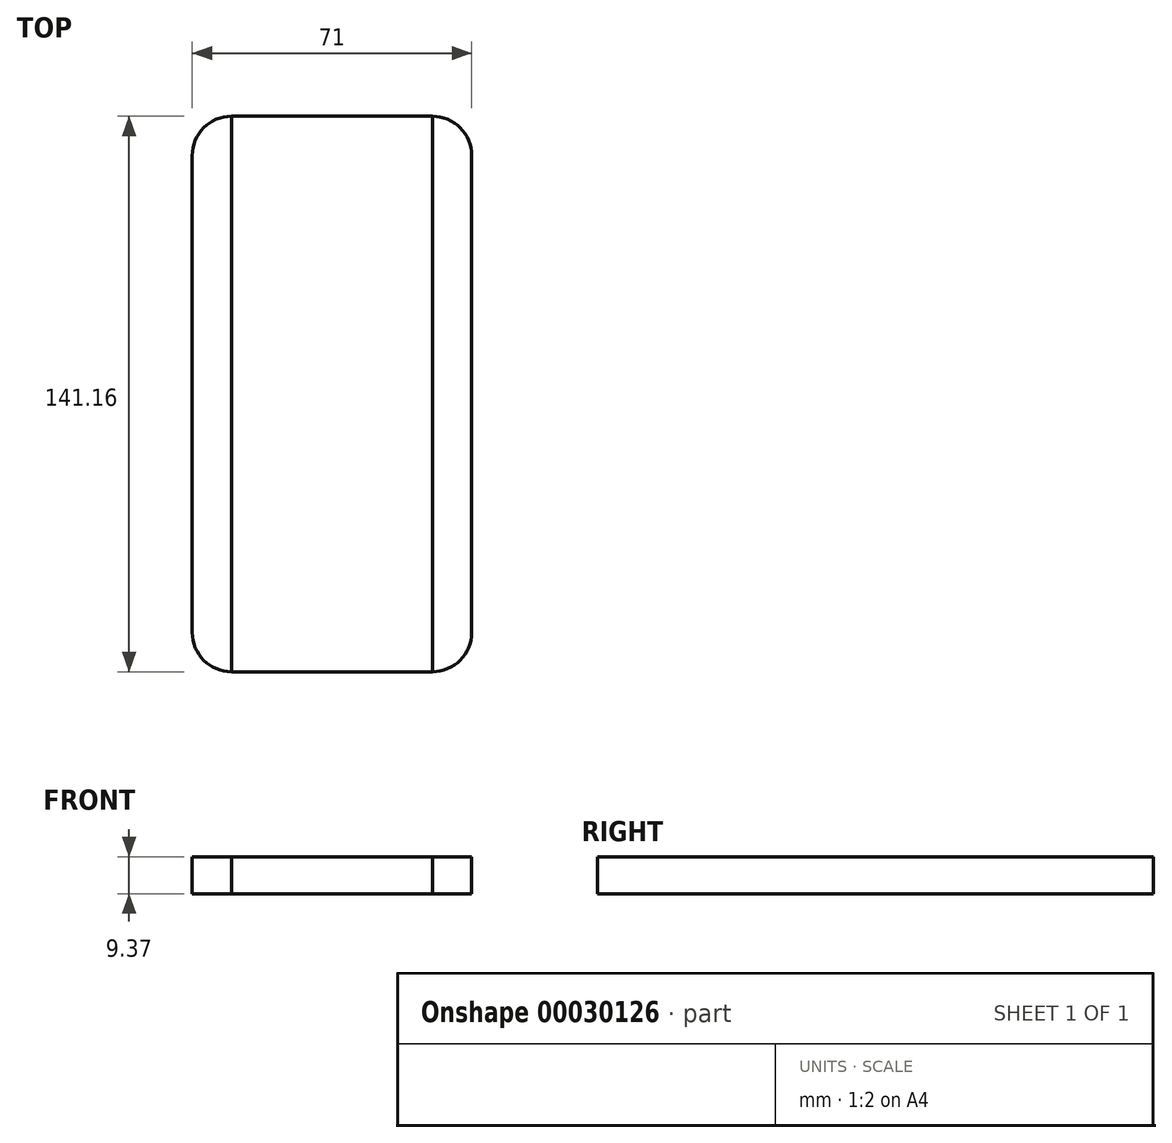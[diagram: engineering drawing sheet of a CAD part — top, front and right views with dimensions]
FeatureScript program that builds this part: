
annotation { "Feature Type Name" : "Feature", "Feature Type Description" : "" }
export const myFeature = defineFeature(function(context is Context, id is Id, definition is map)
    precondition{}
    {
        {
            var Q0;
            Q0=qCreatedBy(makeId("Top.planeOp"),FACE);
            var sketch = newSketch(context, id + "F0", { "sketchPlane" : qUnion([Q0])});
            skLineSegment(sketch, "E0.rect.bottom", {"start": v(35.5, -70.58) * mm, "end": v(-35.5, -70.58) * mm});
            skLineSegment(sketch, "E0.rect.top", {"start": v(35.5, 70.58) * mm, "end": v(-35.5, 70.58) * mm});
            skLineSegment(sketch, "E0.rect.left", {"start": v(35.5, -70.58) * mm, "end": v(35.5, 70.58) * mm});
            skLineSegment(sketch, "E0.rect.right", {"start": v(-35.5, -70.58) * mm, "end": v(-35.5, 70.57) * mm});
            skPoint(sketch, "E0.rect.middle", {"position": v(0, 0) * mm});
            skSolve(sketch);
        }
        {
            var Q0;
            Q0=makeQuery(id+"F0.imprint","IMPRINT",FACE,{"disambiguationData":[TD([[makeQuery(id+"F0.imprint","IMPRINT",EDGE,{"derivedFrom":sQuery(id+"F0.wireOp",EDGE,"E0.rect.bottom")}),-1.0]])]});
            extrude(context, id + "F1", {"entities" : qUnion([Q0]), "depth" : 9.37 * mm});
        }
        {
            var Q0;
            Q0=makeQuery(id+"F1.opExtrude","SWEPT_EDGE",EDGE,{"disambiguationData":[OSD([sQuery(id+"F0.wireOp",EDGE,"E0.rect.bottom"),sQuery(id+"F0.wireOp",EDGE,"E0.rect.left")])]});
            var Q1;
            Q1=makeQuery(id+"F1.opExtrude","SWEPT_EDGE",EDGE,{"disambiguationData":[OSD([sQuery(id+"F0.wireOp",EDGE,"E0.rect.bottom"),sQuery(id+"F0.wireOp",EDGE,"E0.rect.right")])]});
            var Q2;
            Q2=makeQuery(id+"F1.opExtrude","SWEPT_EDGE",EDGE,{"disambiguationData":[OSD([sQuery(id+"F0.wireOp",EDGE,"E0.rect.top"),sQuery(id+"F0.wireOp",EDGE,"E0.rect.left")])]});
            var Q3;
            Q3=makeQuery(id+"F1.opExtrude","SWEPT_EDGE",EDGE,{"disambiguationData":[OSD([sQuery(id+"F0.wireOp",EDGE,"E0.rect.top"),sQuery(id+"F0.wireOp",EDGE,"E0.rect.right")])]});
            fillet(context, id + "F2", {"entities" : qUnion([Q0, Q1, Q2, Q3]), "radius" : 10 * mm, "tangentPropagation" : true, "allowEdgeOverflow" : false});
        }
        {
            var Q0;
            Q0=makeQuery(id+"F1.opExtrude","CAP_FACE",FACE,{"disambiguationData":[OSD([sQuery(id+"F0.wireOp",EDGE,"E0.rect.bottom"),sQuery(id+"F0.wireOp",EDGE,"E0.rect.top"),sQuery(id+"F0.wireOp",EDGE,"E0.rect.left"),sQuery(id+"F0.wireOp",EDGE,"E0.rect.right")])],"isStart":false});
            var sketch = newSketch(context, id + "F3", { "sketchPlane" : qUnion([Q0])});
            skLineSegment(sketch, "E1", {"start": v(-25.5, 70.58) * mm, "end": v(-25.5, -70.58) * mm});
            skLineSegment(sketch, "E2", {"start": v(-25.5, -70.58) * mm, "end": v(25.5, -70.58) * mm});
            skLineSegment(sketch, "E3", {"start": v(25.5, -70.58) * mm, "end": v(25.5, 70.58) * mm});
            skLineSegment(sketch, "E4", {"start": v(25.5, 70.58) * mm, "end": v(-25.5, 70.58) * mm});
            skSolve(sketch);
        }
        {
            var Q0;
            Q0=makeQuery(id+"F3.imprint","IMPRINT",FACE,{"disambiguationData":[TD([[makeQuery(id+"F3.imprint","IMPRINT",EDGE,{"derivedFrom":sQuery(id+"F3.wireOp",EDGE,"E1")}),-1.0]])]});
            var Q1;
            Q1=makeQuery(id+"F3.imprint","IMPRINT",FACE,{"disambiguationData":[TD([[makeQuery(id+"F3.imprint","IMPRINT",EDGE,{"derivedFrom":sQuery(id+"F3.wireOp",EDGE,"E3")}),-1.0]])]});
            extrude(context, id + "F4", {"entities" : qUnion([Q0, Q1]), "oppositeDirection" : true, "depth" : 9.37 * mm});
        }
        {
            var Q0;
            Q0=makeQuery(id+"F3.imprint","IMPRINT",FACE,{"disambiguationData":[TD([[makeQuery(id+"F3.imprint","IMPRINT",EDGE,{"derivedFrom":sQuery(id+"F3.wireOp",EDGE,"E1")}),1.0]])]});
            extrude(context, id + "F5", {"entities" : qUnion([Q0]), "oppositeDirection" : true, "depth" : 9.37 * mm});
        }
    });
